# Revit family: RN 57024 Optifitt-Press-Muffe
name_source: partatom
category: Rohrformteile
units: mm (PartAtom-declared; Revit-internal decimal feet)

## family parameters
Arbeitsebenenbasiert = Nein
Beim Laden mit Abzugskörper schneiden = Nein
Bemaßung runder Anschluss = Durchmesser verwenden
Gemeinsam genutzt = Nein
Immer vertikal = Ja
Teiletyp = Verbindung

## types (2) — shared parameters
1.010.00.2 Blattnummer der Richtlinie = 29
1.010.00.3 Ausgabedatum (Monat) der Richtlinie = 201308
1.010.00.4 Herstellername = R. Nussbaum AG
1.010.00.5 Revisionsdatum der Datei = 20190521
1.010.00.6 Webadresse des Herstellers = http://www.nussbaum.ch
1.100.00.4 Produktbezeichnung = Versorgung
1.110.00.2 Index = 2
1.110.00.4 Produktbezeichnung = Optifitt-Press
1.960/3L.00.8 Link (URL) = https://www.nussbaum.ch
29.700.00.4 Produktname = Optifitt-Press-Muffe, auf Siederohre
29.700.00.5 Produktkennung = 2
29.700.00.6 Querschnittsform = 1
29.700.00.7 Nennweitensystem = DN
29.700.00.8 Nenndrucksystem = PN
29.710.02.4 Nenndruck = 16
29.710.02.5 max. zul. Überdruck [hPa] = 1600
29.710.02.7 max. zul. Dauer-Betriebsdruck [hPa] = 1600
29.710.02.9 max. zul. Dauer-Betriebstemperatur [°C] = 95
Beschreibung = Optifitt-Press-Muffe
Connector Visibility = Nein
EnclosingSpace Visibility = Nein
Hersteller = R. Nussbaum AG
URL = https://www.nussbaum.ch

## per-type parameters (varying)
| type | 1.800.00.3 TGA-Nummer | 1.800.00.4 Kommentarfeld | 1.810.00.3 Hersteller-Bestellnummer | 1.810.00.4 DATANORM-Nummer | 1.810.00.6 GTIN-Nummer | 29.710.02.10 Formstück-Gewicht [kg] | 29.710.02.3 Benennung | CONNECTOR0_DIAMETER_dX_0r | CONNECTOR0_dX_01 | CONNECTOR0_ref_dX | CONNECTOR1_DIAMETER_dX_0r | CONNECTOR1_dX_00 | CONNECTOR1_dX_01 | CONNECTOR1_ref_dX | Modell | R. Nussbaum AG 57024.27 de Visibility | R. Nussbaum AG 57024.28 de Visibility | Typenkommentare |
| DN=50 | 01900200000000000000000000000000000000000000000011000000000000000002 | 57024.28, Optifitt-Press-Muffe, auf Siederohre, DN=50, L=120 | 57024.28 | 57024.28 | 7612945746160 | 0.665 | Optifitt-Press-Muffe, auf Siederohre, DN=50, L=120 | 50 mm | 50 mm | 50 mm | 50 mm | 72 mm | 120 mm | 72 mm | 57024.28 | Nein | Ja | Optifitt-Press-Muffe  DN=50 |
| DN=40 | 01900200000000000000000000000000000000000000000011000000000000000001 | 57024.27, Optifitt-Press-Muffe, auf Siederohre, DN=40, L=114 | 57024.27 | 57024.27 | 7612945746153 | 0.502 | Optifitt-Press-Muffe, auf Siederohre, DN=40, L=114 | 40 mm | 48 mm | 48 mm | 40 mm | 66 mm | 114 mm | 66 mm | 57024.27 | Ja | Nein | Optifitt-Press-Muffe  DN=40 |

## geometry (parser evidence)
native form markers: Sweep x2
no freeform markers — native parametric forms only
